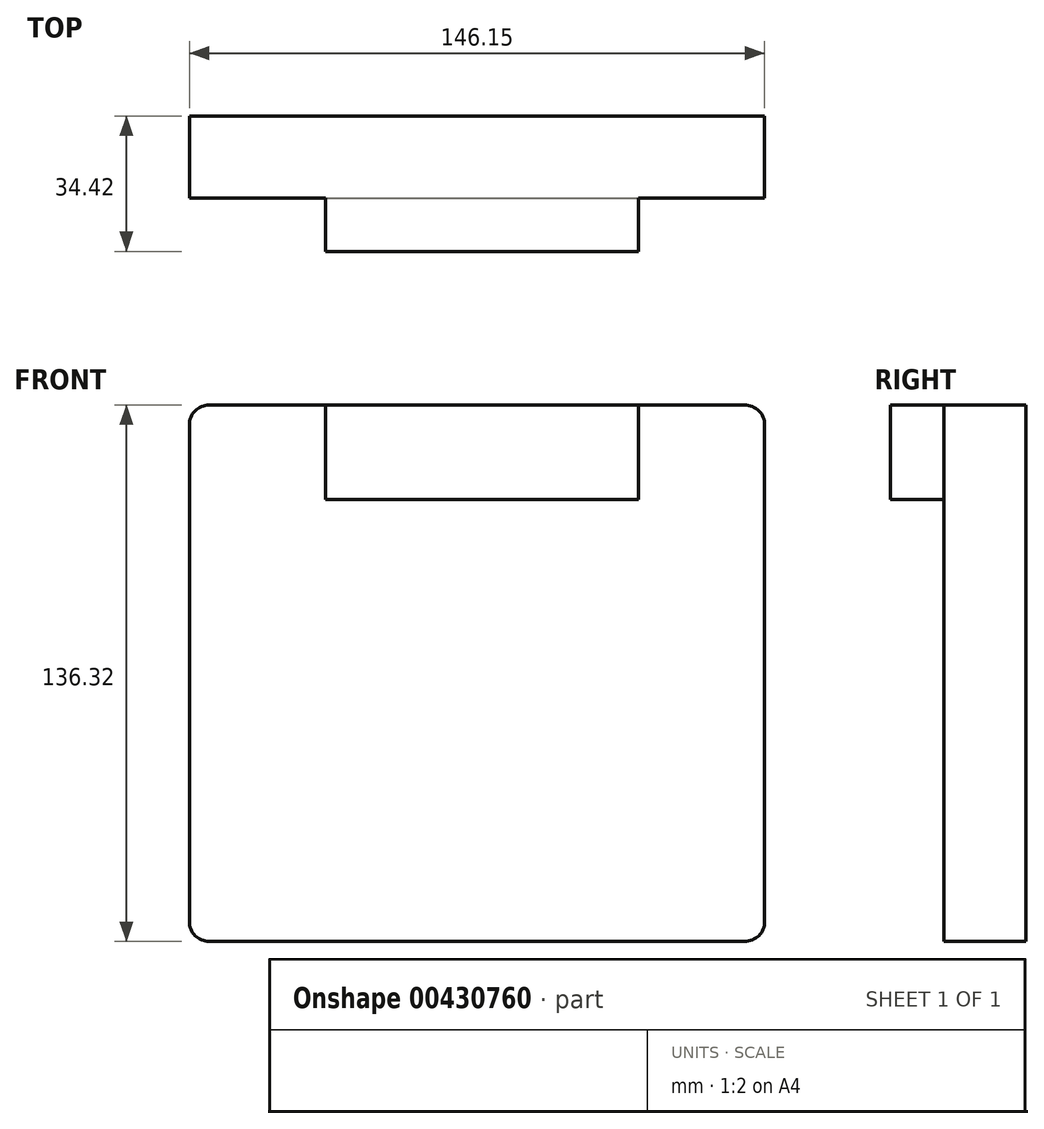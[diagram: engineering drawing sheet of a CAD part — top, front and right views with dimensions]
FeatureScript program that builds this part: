
annotation { "Feature Type Name" : "Feature", "Feature Type Description" : "" }
export const myFeature = defineFeature(function(context is Context, id is Id, definition is map)
    precondition{}
    {
        {
            var Q0;
            Q0=qCreatedBy(makeId("Front.planeOp"),FACE);
            var sketch = newSketch(context, id + "F0", { "sketchPlane" : qUnion([Q0])});
            skLineSegment(sketch, "E0.bottom", {"start": v(-76.25, -66.57) * mm, "end": v(69.9, -66.57) * mm});
            skLineSegment(sketch, "E0.top", {"start": v(-76.25, 69.75) * mm, "end": v(69.9, 69.75) * mm});
            skLineSegment(sketch, "E0.left", {"start": v(-76.25, -66.57) * mm, "end": v(-76.25, 69.75) * mm});
            skLineSegment(sketch, "E0.right", {"start": v(69.9, -66.57) * mm, "end": v(69.9, 69.75) * mm});
            skSolve(sketch);
        }
        {
            var Q0;
            Q0=makeQuery(id+"F0.imprint","IMPRINT",FACE,{"disambiguationData":[TD([[makeQuery(id+"F0.imprint","IMPRINT",EDGE,{"derivedFrom":sQuery(id+"F0.wireOp",EDGE,"E0.bottom")}),1.0]])]});
            extrude(context, id + "F1", {"entities" : qUnion([Q0]), "depth" : 20.9 * mm});
        }
        {
            var Q0;
            Q0=makeQuery(id+"F1.opExtrude","CAP_FACE",FACE,{"disambiguationData":[OSD([sQuery(id+"F0.wireOp",EDGE,"E0.bottom"),sQuery(id+"F0.wireOp",EDGE,"E0.top"),sQuery(id+"F0.wireOp",EDGE,"E0.left"),sQuery(id+"F0.wireOp",EDGE,"E0.right")])],"isStart":false});
            var sketch = newSketch(context, id + "F2", { "sketchPlane" : qUnion([Q0])});
            skLineSegment(sketch, "E1.bottom", {"start": v(-41.62, 69.75) * mm, "end": v(37.9, 69.75) * mm});
            skLineSegment(sketch, "E1.top", {"start": v(-41.62, 45.75) * mm, "end": v(37.9, 45.75) * mm});
            skLineSegment(sketch, "E1.left", {"start": v(-41.62, 69.75) * mm, "end": v(-41.62, 45.75) * mm});
            skLineSegment(sketch, "E1.right", {"start": v(37.9, 69.75) * mm, "end": v(37.9, 45.75) * mm});
            skSolve(sketch);
        }
        {
            var Q0;
            Q0=makeQuery(id+"F2.imprint","IMPRINT",FACE,{"disambiguationData":[TD([[makeQuery(id+"F2.imprint","IMPRINT",EDGE,{"derivedFrom":sQuery(id+"F2.wireOp",EDGE,"E1.bottom")}),-1.0]])]});
            extrude(context, id + "F3", {"entities" : qUnion([Q0]), "operationType" : NewBodyOperationType.ADD, "depth" : 13.5 * mm});
        }
        {
            var Q0;
            Q0=makeQuery(id+"F1.opExtrude","SWEPT_EDGE",EDGE,{"disambiguationData":[OSD([sQuery(id+"F0.wireOp",EDGE,"E0.bottom"),sQuery(id+"F0.wireOp",EDGE,"E0.right")])]});
            var Q1;
            Q1=makeQuery(id+"F1.opExtrude","SWEPT_EDGE",EDGE,{"disambiguationData":[OSD([sQuery(id+"F0.wireOp",EDGE,"E0.top"),sQuery(id+"F0.wireOp",EDGE,"E0.right")])]});
            var Q2;
            Q2=makeQuery(id+"F1.opExtrude","SWEPT_EDGE",EDGE,{"disambiguationData":[OSD([sQuery(id+"F0.wireOp",EDGE,"E0.top"),sQuery(id+"F0.wireOp",EDGE,"E0.left")])]});
            var Q3;
            Q3=makeQuery(id+"F1.opExtrude","SWEPT_EDGE",EDGE,{"disambiguationData":[OSD([sQuery(id+"F0.wireOp",EDGE,"E0.bottom"),sQuery(id+"F0.wireOp",EDGE,"E0.left")])]});
            fillet(context, id + "F4", {"entities" : qUnion([Q0, Q1, Q2, Q3]), "radius" : 5.08 * mm, "tangentPropagation" : true, "allowEdgeOverflow" : false});
        }
    });
